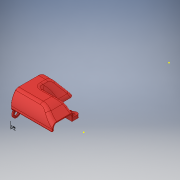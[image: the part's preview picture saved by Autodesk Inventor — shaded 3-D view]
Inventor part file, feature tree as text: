
AUTODESK INVENTOR PART (.ipt)
format: ipt  version: 2019.4 (Build 234330000, 330)  size: 2,782,720 bytes
history: native  units: in
note: dims shown in document units (in); Inventor stores cm internally (conversion verified against a paired STEP export)
features: other x7, sketch x7, fillet x6, extrude x4, plane x2, loft x2, projected_geometry x2
ambient origin geometry x8: Origin, YZ Plane, XZ Plane, XY Plane, X Axis, Y Axis, Z Axis, Center Point
bodies: Solid1 (feature_tree)
feature tree (30):
  other  "Annotations"
  plane  "Work Plane1"
  extrude  "Extrusion1"  Depth=0.315in TaperAngle=0.0deg
  plane  "Work Plane2"
  extrude  "Extrusion2"  Depth=0.0197in
  fillet  "Fillet1"  Radius=0.2362in
  extrude  "Extrusion3"  Depth=0.3937in
  fillet  "Fillet2"  Radius=0.3937in
  fillet  "Fillet3"  Radius=0.8661in
  fillet  "Fillet4"  Radius=0.3937in
  fillet  "Fillet5"  Radius=0.3937in
  fillet  "Fillet6"  Radius=0.2362in
  extrude  "Extrusion4"  Depth=0.1969in
  loft  "Loft1"
  sketch  "Sketch6"  dims[d25=0.2362in d26=0.1969in]
  sketch  "Sketch8"  dims[d27=0.1575in d28=0.3937in d29=0.0in]
  sketch  "Sketch9"  dims[d30=0.0157in d31=0.0157in]
  loft  "Loft2"
  sketch  "Sketch3"  dims[d4=-0.0394in d5=0.315in d6=0.0in]
  sketch  "Sketch4"  dims[d7=0.2756in d8=0.0in d15=0.0197in d16=0.2362in]
  sketch  "Sketch5"  dims[d17=0.2362in d18=0.3937in d19=0.3937in d20=0.8661in d22=0.3937in d23=0.3937in d24=0.2362in]
  other  "Edges1"
  other  "Edges3"
  sketch  "Sketch10"  dims[d32=0.315in d33=0.315in d34=0.0591in d37=0.2362in d38=0.0in d39=0.0in d40=90.0deg d44=90.0deg d45=0.0in d46=90.0deg d52=0.0197in d54=0.0in d55=90.0deg d56=0.0in d57=90.0deg d10=0.1674in d11=0.0787in d12=-0.4302in d13=-0.17in d14=0.2362in d9=0.2838in]
  other  "Edges4"
  other  "[a]_connector_cover"
  projected_geometry  "Project Cut Edges1"
  projected_geometry  "Project Cut Edges2"
  other  "Linear Dimension 1"
  other  "Linear Dimension 2"
